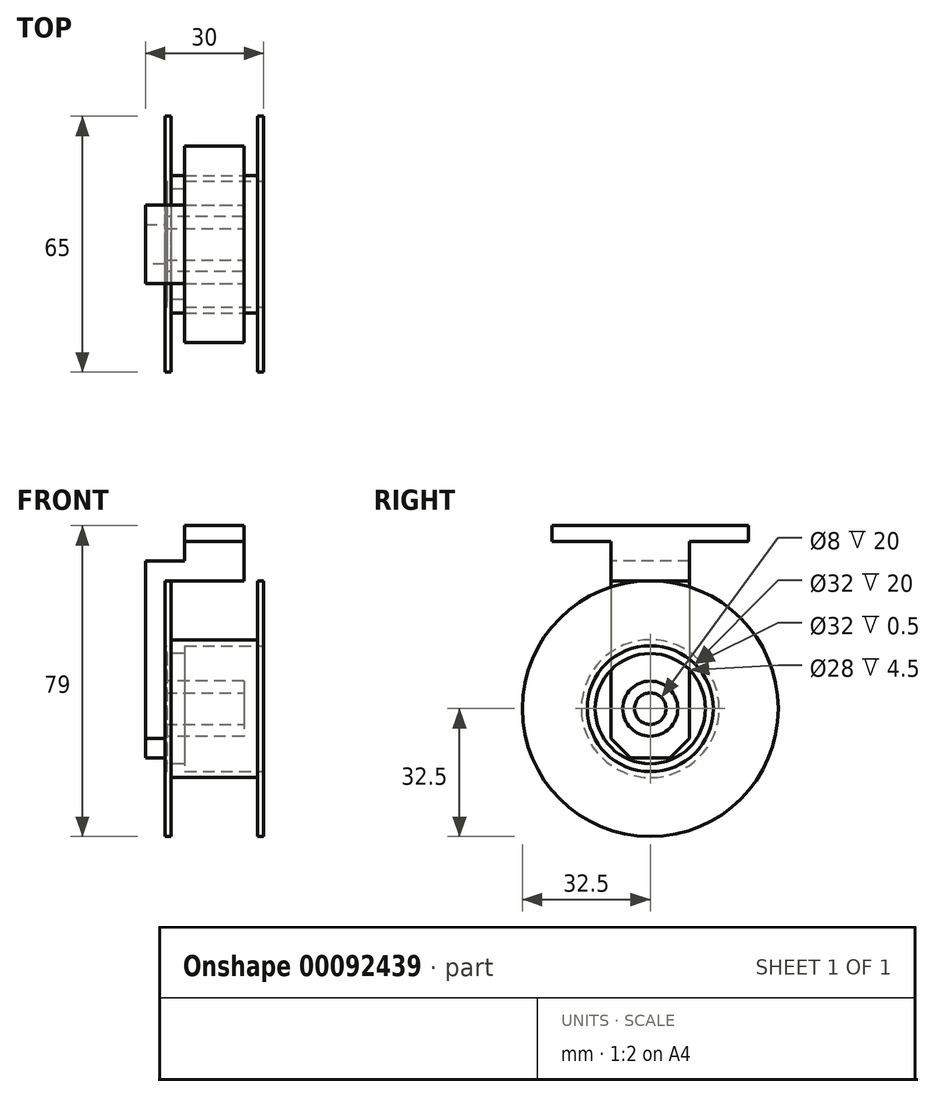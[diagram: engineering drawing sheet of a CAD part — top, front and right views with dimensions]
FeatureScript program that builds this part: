
annotation { "Feature Type Name" : "Feature", "Feature Type Description" : "" }
export const myFeature = defineFeature(function(context is Context, id is Id, definition is map)
    precondition{}
    {
        {
            var Q0;
            Q0=qCreatedBy(makeId("Right.planeOp"),FACE);
            var sketch = newSketch(context, id + "F0", { "sketchPlane" : qUnion([Q0])});
            skCircle(sketch, "E0", {"center": v(0, 0) * mm, "radius": 32.5 * mm});
            skSolve(sketch);
        }
        {
            var Q0;
            Q0=makeQuery(id+"F0.imprint","IMPRINT",FACE,{"disambiguationData":[TD([[makeQuery(id+"F0.imprint","IMPRINT",EDGE,{"derivedFrom":sQuery(id+"F0.wireOp",EDGE,"E0")}),1.0]])]});
            extrude(context, id + "F1", {"entities" : qUnion([Q0]), "endBound" : BoundingType.SYMMETRIC, "depth" : 25 * mm});
        }
        {
            var Q0;
            Q0=qCreatedBy(makeId("Front.planeOp"),FACE);
            var sketch = newSketch(context, id + "F2", { "sketchPlane" : qUnion([Q0])});
            skLineSegment(sketch, "E1", {"start": v(-12.5, 32.5) * mm, "end": v(7.5, 32.5) * mm});
            skLineSegment(sketch, "E2", {"start": v(-12.5, 32.5) * mm, "end": v(-12.5, -12.5) * mm});
            skLineSegment(sketch, "E3.0", {"start": v(-17.5, 37.5) * mm, "end": v(-17.5, -12.5) * mm});
            skLineSegment(sketch, "E4.0", {"start": v(-17.5, 37.5) * mm, "end": v(7.5, 37.5) * mm});
            skLineSegment(sketch, "E5.filletArc", {"start": v(-17.5, 37.5) * mm, "end": v(-17.5, 37.5) * mm});
            skLineSegment(sketch, "E6", {"start": v(-17.5, -12.5) * mm, "end": v(-12.5, -12.5) * mm});
            skLineSegment(sketch, "E7.bottom", {"start": v(-7.5, 46.5) * mm, "end": v(7.5, 46.5) * mm});
            skLineSegment(sketch, "E7.top", {"start": v(-7.5, 42.5) * mm, "end": v(7.5, 42.5) * mm});
            skLineSegment(sketch, "E7.left", {"start": v(-7.5, 46.5) * mm, "end": v(-7.5, 42.5) * mm});
            skLineSegment(sketch, "E7.right", {"start": v(7.5, 46.5) * mm, "end": v(7.5, 42.5) * mm});
            skLineSegment(sketch, "E8", {"start": v(0, 46.5) * mm, "end": v(0, 42.5) * mm});
            skLineSegment(sketch, "E9", {"start": v(7.5, 37.5) * mm, "end": v(7.5, 32.5) * mm});
            skPoint(sketch, "E10.start.orphan", {"position": v(12.5, 32.5) * mm});
            skSolve(sketch);
        }
        {
            var Q0;
            Q0=makeQuery(id+"F2.imprint","IMPRINT",FACE,{"disambiguationData":[TD([[makeQuery(id+"F2.imprint","IMPRINT",EDGE,{"derivedFrom":sQuery(id+"F2.wireOp",EDGE,"E1")}),1.0]])]});
            extrude(context, id + "F3", {"entities" : qUnion([Q0]), "endBound" : BoundingType.SYMMETRIC, "depth" : 20 * mm});
        }
        {
            var Q0;
            {var subQ0=sQuery(id+"F2.wireOp",EDGE,"E7.left");Q0=makeQuery(id+"F2.imprint","IMPRINT",FACE,{"disambiguationData":[TD([[makeQuery(id+"F2.imprint","IMPRINT",EDGE,{"derivedFrom":subQ0}),1.0]])]});}
            var Q1;
            {var subQ0=sQuery(id+"F2.wireOp",EDGE,"E7.right");Q1=makeQuery(id+"F2.imprint","IMPRINT",FACE,{"disambiguationData":[TD([[makeQuery(id+"F2.imprint","IMPRINT",EDGE,{"derivedFrom":subQ0}),-1.0]])]});}
            extrude(context, id + "F4", {"entities" : qUnion([Q0, Q1]), "endBound" : BoundingType.SYMMETRIC, "depth" : 50 * mm});
        }
        {
            var Q0;
            Q0=makeQuery(id+"F4.opExtrude","SWEPT_FACE",FACE,{"disambiguationData":[OSD([sQuery(id+"F2.wireOp",EDGE,"E7.bottom")])]});
            var sketch = newSketch(context, id + "F5", { "sketchPlane" : qUnion([Q0])});
            skLineSegment(sketch, "E11", {"start": v(-7.5, 10) * mm, "end": v(-7.5, -10) * mm});
            skLineSegment(sketch, "E12.0", {"start": v(-7.5, -10) * mm, "end": v(7.5, -10) * mm});
            skLineSegment(sketch, "E13.0", {"start": v(-7.5, 10) * mm, "end": v(7.5, 10) * mm});
            skLineSegment(sketch, "E14.0", {"start": v(7.5, -10) * mm, "end": v(7.5, 10) * mm});
            skPoint(sketch, "E15.orphan", {"position": v(7.5, 25) * mm});
            skPoint(sketch, "E16.orphan", {"position": v(-17.5, 10) * mm});
            skPoint(sketch, "E17.orphan", {"position": v(-17.5, -10) * mm});
            skPoint(sketch, "E18.orphan", {"position": v(7.5, -25) * mm});
            skSolve(sketch);
        }
        {
            var Q0;
            Q0=makeQuery(id+"F5.imprint","IMPRINT",FACE,{"disambiguationData":[TD([[makeQuery(id+"F5.imprint","IMPRINT",EDGE,{"derivedFrom":sQuery(id+"F5.wireOp",EDGE,"E11")}),-1.0]])]});
            var Q1;
            Q1=makeQuery(id+"F3.opExtrude","SWEPT_FACE",FACE,{"disambiguationData":[OSD([sQuery(id+"F2.wireOp",EDGE,"E4.0")])]});
            extrude(context, id + "F6", {"entities" : qUnion([Q0]), "operationType" : NewBodyOperationType.ADD, "endBound" : BoundingType.UP_TO_SURFACE, "oppositeDirection" : true, "endBoundEntityFace" : qUnion([Q1]), "depth" : 9 * mm});
        }
        {
            var Q0;
            Q0=makeQuery(id+"F1.opExtrude","CAP_FACE",FACE,{"disambiguationData":[OSD([sQuery(id+"F0.wireOp",EDGE,"E0")])],"isStart":false});
            var sketch = newSketch(context, id + "F7", { "sketchPlane" : qUnion([Q0])});
            skCircle(sketch, "E19", {"center": v(0, 0) * mm, "radius": 4 * mm});
            skCircle(sketch, "E20.0", {"center": v(0, 0) * mm, "radius": 32.5 * mm});
            skCircle(sketch, "E21.0", {"center": v(0, 0) * mm, "radius": 17.5 * mm});
            skCircle(sketch, "E22.0", {"center": v(0, 0) * mm, "radius": 16 * mm});
            skSolve(sketch);
        }
        {
            var Q0;
            Q0=makeQuery(id+"F7.imprint","IMPRINT",FACE,{"disambiguationData":[TD([[makeQuery(id+"F7.imprint","IMPRINT",EDGE,{"derivedFrom":sQuery(id+"F7.wireOp",EDGE,"E19")}),1.0]])]});
            var Q1;
            Q1=makeQuery(id+"F3.opExtrude","SWEPT_FACE",FACE,{"disambiguationData":[OSD([sQuery(id+"F2.wireOp",EDGE,"E2")])]});
            extrude(context, id + "F8", {"entities" : qUnion([Q0]), "endBound" : BoundingType.UP_TO_SURFACE, "oppositeDirection" : true, "endBoundEntityFace" : qUnion([Q1]), "depth" : 25 * mm});
        }
        {
            var Q0;
            Q0=makeQuery(id+"F7.imprint","IMPRINT",FACE,{"disambiguationData":[TD([[makeQuery(id+"F7.imprint","IMPRINT",EDGE,{"derivedFrom":sQuery(id+"F7.wireOp",EDGE,"E20.0")}),1.0]])]});
            extrude(context, id + "F9", {"entities" : qUnion([Q0]), "operationType" : NewBodyOperationType.REMOVE, "oppositeDirection" : true, "depth" : 23.5 * mm, "hasSecondDirection" : true, "secondDirectionOppositeDirection" : true, "secondDirectionDepth" : 1.5 * mm});
        }
        {
            var Q0;
            Q0=makeQuery(id+"F7.imprint","IMPRINT",FACE,{"disambiguationData":[TD([[makeQuery(id+"F7.imprint","IMPRINT",EDGE,{"derivedFrom":sQuery(id+"F7.wireOp",EDGE,"E19")}),-1.0]])]});
            var Q1;
            Q1=makeQuery(id+"F7.imprint","IMPRINT",FACE,{"disambiguationData":[TD([[makeQuery(id+"F7.imprint","IMPRINT",EDGE,{"derivedFrom":sQuery(id+"F7.wireOp",EDGE,"E19")}),1.0]])]});
            extrude(context, id + "F10", {"entities" : qUnion([Q0, Q1]), "operationType" : NewBodyOperationType.REMOVE, "oppositeDirection" : true, "depth" : 25 * mm});
        }
        {
            var Q0;
            Q0=makeQuery(id+"F3.opExtrude","CAP_EDGE",EDGE,{"disambiguationData":[OSD([sQuery(id+"F2.wireOp",EDGE,"E6")])],"isStart":true});
            var Q1;
            Q1=makeQuery(id+"F3.opExtrude","CAP_EDGE",EDGE,{"disambiguationData":[OSD([sQuery(id+"F2.wireOp",EDGE,"E6")])],"isStart":false});
            chamfer(context, id + "F11", {"entities" : qUnion([Q0, Q1]), "width" : 5 * mm, "tangentPropagation" : true});
        }
        {
            var Q0;
            Q0=makeQuery(id+"F1.opExtrude","CAP_FACE",FACE,{"disambiguationData":[OSD([sQuery(id+"F0.wireOp",EDGE,"E0")])],"isStart":true});
            var sketch = newSketch(context, id + "F12", { "sketchPlane" : qUnion([Q0])});
            skCircle(sketch, "E23.0", {"center": v(0, 0) * mm, "radius": 16 * mm});
            skCircle(sketch, "E24.0", {"center": v(0, 0) * mm, "radius": 14 * mm});
            skCircle(sketch, "E25", {"center": v(0, 0) * mm, "radius": 7 * mm});
            skSolve(sketch);
        }
        {
            var Q0;
            Q0=makeQuery(id+"F12.imprint","IMPRINT",FACE,{"disambiguationData":[TD([[makeQuery(id+"F12.imprint","IMPRINT",EDGE,{"derivedFrom":sQuery(id+"F12.wireOp",EDGE,"E23.0")}),-1.0]])]});
            extrude(context, id + "F13", {"entities" : qUnion([Q0]), "operationType" : NewBodyOperationType.ADD, "oppositeDirection" : true, "depth" : 2.5 * mm, "hasSecondDirection" : true, "secondDirectionOppositeDirection" : true, "secondDirectionDepth" : 0.5 * mm});
        }
        {
            var Q0;
            Q0=makeQuery(id+"F12.imprint","IMPRINT",FACE,{"disambiguationData":[TD([[makeQuery(id+"F12.imprint","IMPRINT",EDGE,{"derivedFrom":sQuery(id+"F12.wireOp",EDGE,"E24.0")}),-1.0]])]});
            var Q1;
            Q1=makeQuery(id+"F12.imprint","IMPRINT",FACE,{"disambiguationData":[TD([[makeQuery(id+"F12.imprint","IMPRINT",EDGE,{"derivedFrom":sQuery(id+"F12.wireOp",EDGE,"E25")}),1.0]])]});
            var Q2;
            Q2=makeQuery(id+"F12.imprint","IMPRINT",FACE,{"disambiguationData":[TD([[makeQuery(id+"F12.imprint","IMPRINT",EDGE,{"derivedFrom":sQuery(id+"F12.wireOp",EDGE,"E23.0")}),-1.0]])]});
            var Q3;
            Q3=makeQuery(id+"F13.opExtrude","CAP_FACE",FACE,{"disambiguationData":[OSD([sQuery(id+"F12.wireOp",EDGE,"E23.0"),sQuery(id+"F12.wireOp",EDGE,"E24.0")])],"isStart":false});
            extrude(context, id + "F14", {"entities" : qUnion([Q0, Q1, Q2]), "operationType" : NewBodyOperationType.ADD, "oppositeDirection" : true, "depth" : 5 * mm, "hasSecondDirection" : true, "secondDirectionBound" : SecondDirectionBoundingType.UP_TO_SURFACE, "secondDirectionOppositeDirection" : true, "secondDirectionBoundEntityFace" : qUnion([Q3]), "secondDirectionDepth" : 25 * mm});
        }
        {
            var Q0;
            Q0=makeQuery(id+"F12.imprint","IMPRINT",FACE,{"disambiguationData":[TD([[makeQuery(id+"F12.imprint","IMPRINT",EDGE,{"derivedFrom":sQuery(id+"F12.wireOp",EDGE,"E25")}),1.0]])]});
            extrude(context, id + "F15", {"entities" : qUnion([Q0]), "operationType" : NewBodyOperationType.ADD, "oppositeDirection" : true, "depth" : 20 * mm});
        }
        {
            var Q0;
            Q0=makeQuery(id+"F7.imprint","IMPRINT",FACE,{"disambiguationData":[TD([[makeQuery(id+"F7.imprint","IMPRINT",EDGE,{"derivedFrom":sQuery(id+"F7.wireOp",EDGE,"E19")}),1.0]])]});
            extrude(context, id + "F16", {"entities" : qUnion([Q0]), "operationType" : NewBodyOperationType.REMOVE, "oppositeDirection" : true, "depth" : 25 * mm});
        }
    });
